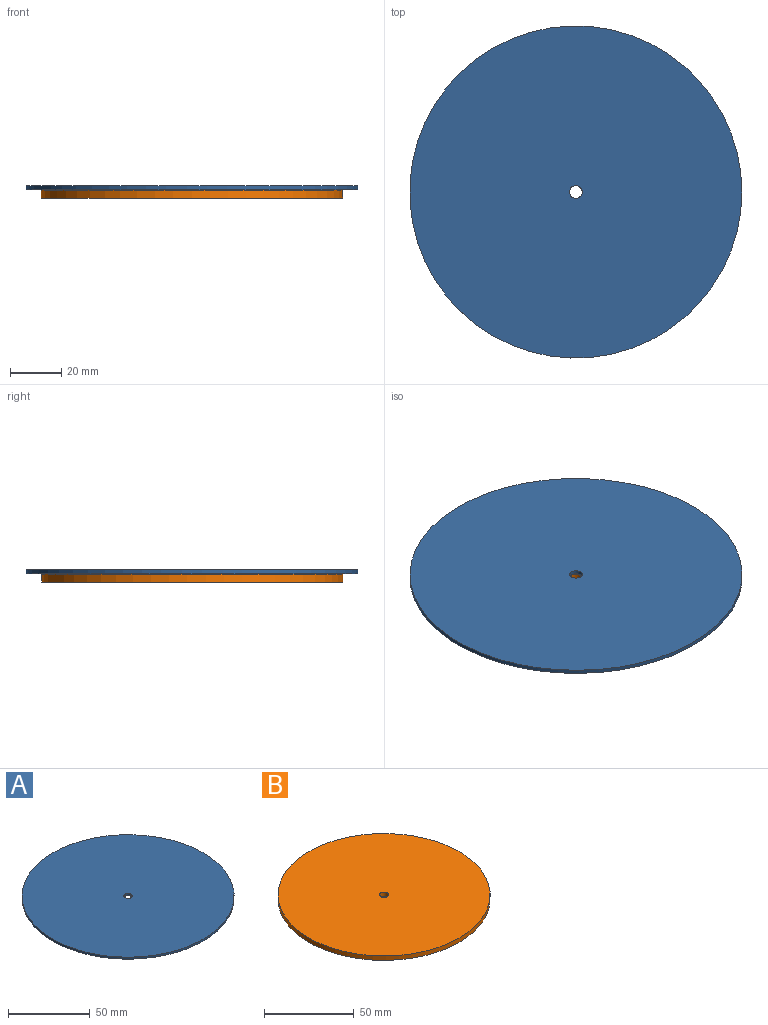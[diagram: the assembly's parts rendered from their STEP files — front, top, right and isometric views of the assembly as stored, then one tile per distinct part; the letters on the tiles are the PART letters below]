
ASSEMBLY  parts=2 mates=1
PART A: 4 faces, bbox 130x130x1.5 mm
  f0: cylinder r=2.5mm len=5mm, axis (0,0,-1), area 23.6mm2, adj f2,f3
  f1: cylinder r=65mm len=130mm, axis (0,0,-1), area 612.6mm2, adj f2,f3
  f2: plane 130x130mm, normal (0,0,1), area 13253.6mm2, adj f0,f1
  f3: plane 130x130mm, normal (0,0,-1), area 13253.6mm2, adj f0,f1
PART B: 4 faces, bbox 118x118x3 mm
  f0: cylinder r=2.5mm len=5mm, axis (0,0,-1), area 47.1mm2, adj f2,f3
  f1: cylinder r=59mm len=118mm, axis (0,0,-1), area 1112.1mm2, adj f2,f3
  f2: plane 118x118mm, normal (0,0,1), area 10916.2mm2, adj f0,f1
  f3: plane 118x118mm, normal (0,0,-1), area 10916.2mm2, adj f0,f1
PLACE A rot(axis=(0,0,1),0deg) t=(0,0,-1.5)mm
PLACE B rot(axis=(0,0,-1),132.4deg) t=(0,0,-4.75)mm
MATE revolute B.f1 <-> A.f1  axis (0,0,1) through (0,0,-1.75)mm
